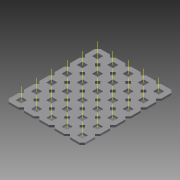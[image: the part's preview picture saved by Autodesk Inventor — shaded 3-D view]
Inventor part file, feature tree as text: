
AUTODESK INVENTOR PART (.ipt)
format: ipt  version: 2015 (Build 190159000, 159)  size: 1,104,384 bytes
history: native  units: in
note: dims shown in document units (in); Inventor stores cm internally (conversion verified against a paired STEP export)
features: other x39, extrude x2, pattern_linear x1, imported_body x1
ambient origin geometry x8: Origin, YZ Plane, XZ Plane, XY Plane, X Axis, Y Axis, Z Axis, Center Point
bodies: Body1 (feature_tree)
feature tree (43):
  other  "Diamond-Pattern"
  other  "Plate"
  extrude  "length cut"  TaperAngle=0.0deg  [1 undecoded]
  extrude  "width cut"  TaperAngle=0.0deg  [1 undecoded]
  other  "constraint axis"
  pattern_linear  "constraint axes"  Spacing1=0.5in  [1 undecoded]
  other  "front plane"
  other  "right plane"
  imported_body  "Base1"
  other  "length profile"
  other  "width profile"
  other  "Work Point1"
  other  "Work Axis36"
  other  "Work Axis37"
  other  "Work Axis38"
  other  "Work Axis39"
  other  "Work Axis40"
  other  "Work Axis41"
  other  "Work Axis42"
  other  "Work Axis43"
  other  "Work Axis44"
  other  "Work Axis45"
  other  "Work Axis46"
  other  "Work Axis47"
  other  "Work Axis48"
  other  "Work Axis49"
  other  "Work Axis50"
  other  "Work Axis51"
  other  "Work Axis52"
  other  "back plane"
  other  "left plane"
  other  "Work Axis120"
  other  "Work Axis121"
  other  "Work Axis122"
  other  "Work Axis123"
  other  "Work Axis124"
  other  "Work Axis125"
  other  "Work Axis126"
  other  "Work Axis127"
  other  "Work Axis128"
  other  "Work Axis129"
  other  "Work Axis130"
  other  "Work Axis131"
note: 3 required parameter values undecoded (feature->parameter linkage not recoverable at this tier; creation-order binding heuristic only, values carry confidence <= 0.55)
